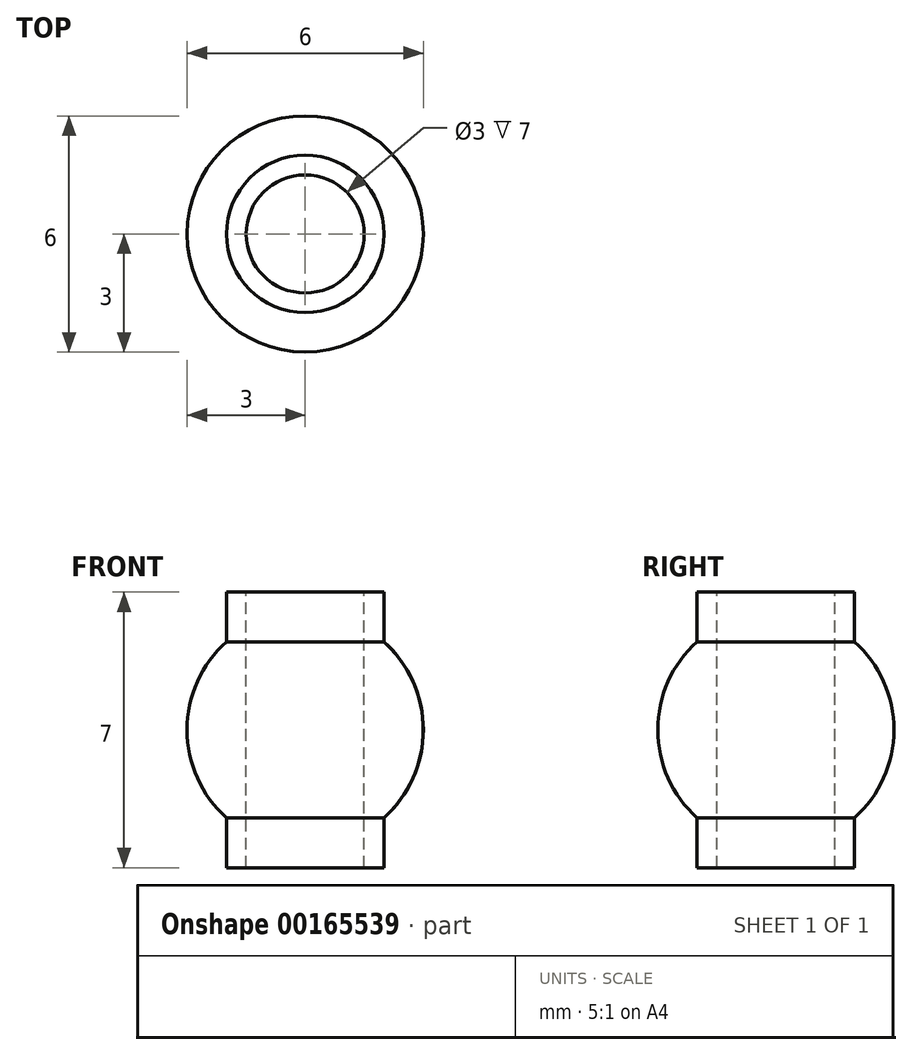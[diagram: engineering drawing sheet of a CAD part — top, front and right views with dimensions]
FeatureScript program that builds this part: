
annotation { "Feature Type Name" : "Feature", "Feature Type Description" : "" }
export const myFeature = defineFeature(function(context is Context, id is Id, definition is map)
    precondition{}
    {
        {
            var Q0;
            Q0=qCreatedBy(makeId("Front.planeOp"),FACE);
            var sketch = newSketch(context, id + "F0", { "sketchPlane" : qUnion([Q0])});
            skLineSegment(sketch, "E0", {"start": v(0, 16.38) * mm, "end": v(0, -19.62) * mm, "construction": true});
            skArc(sketch, "E1", {"start": v(2, -2.24) * mm, "mid": v(3, 0) * mm, "end": v(2, 2.24) * mm});
            skLineSegment(sketch, "E2", {"start": v(1.5, 3.5) * mm, "end": v(1.5, -3.5) * mm});
            skLineSegment(sketch, "E3", {"start": v(2, 3.5) * mm, "end": v(2, 2.24) * mm});
            skLineSegment(sketch, "E4", {"start": v(1.5, 3.5) * mm, "end": v(2, 3.5) * mm});
            skLineSegment(sketch, "E5", {"start": v(1.5, -3.5) * mm, "end": v(2, -3.5) * mm});
            skLineSegment(sketch, "E6.trimOffspring", {"start": v(2, -2.24) * mm, "end": v(2, -3.5) * mm});
            skSolve(sketch);
        }
        {
            var Q0;
            Q0=makeQuery(id+"F0.imprint","IMPRINT",FACE,{"disambiguationData":[TD([[makeQuery(id+"F0.imprint","IMPRINT",EDGE,{"derivedFrom":sQuery(id+"F0.wireOp",EDGE,"E1")}),1.0]])]});
            var Q1;
            Q1=sQuery(id+"F0.wireOp",EDGE,"E0");
            revolve(context, id + "F1", {"entities" : qUnion([Q0]), "axis" : qUnion([Q1]), "revolveType" : RevolveType.FULL});
        }
    });
